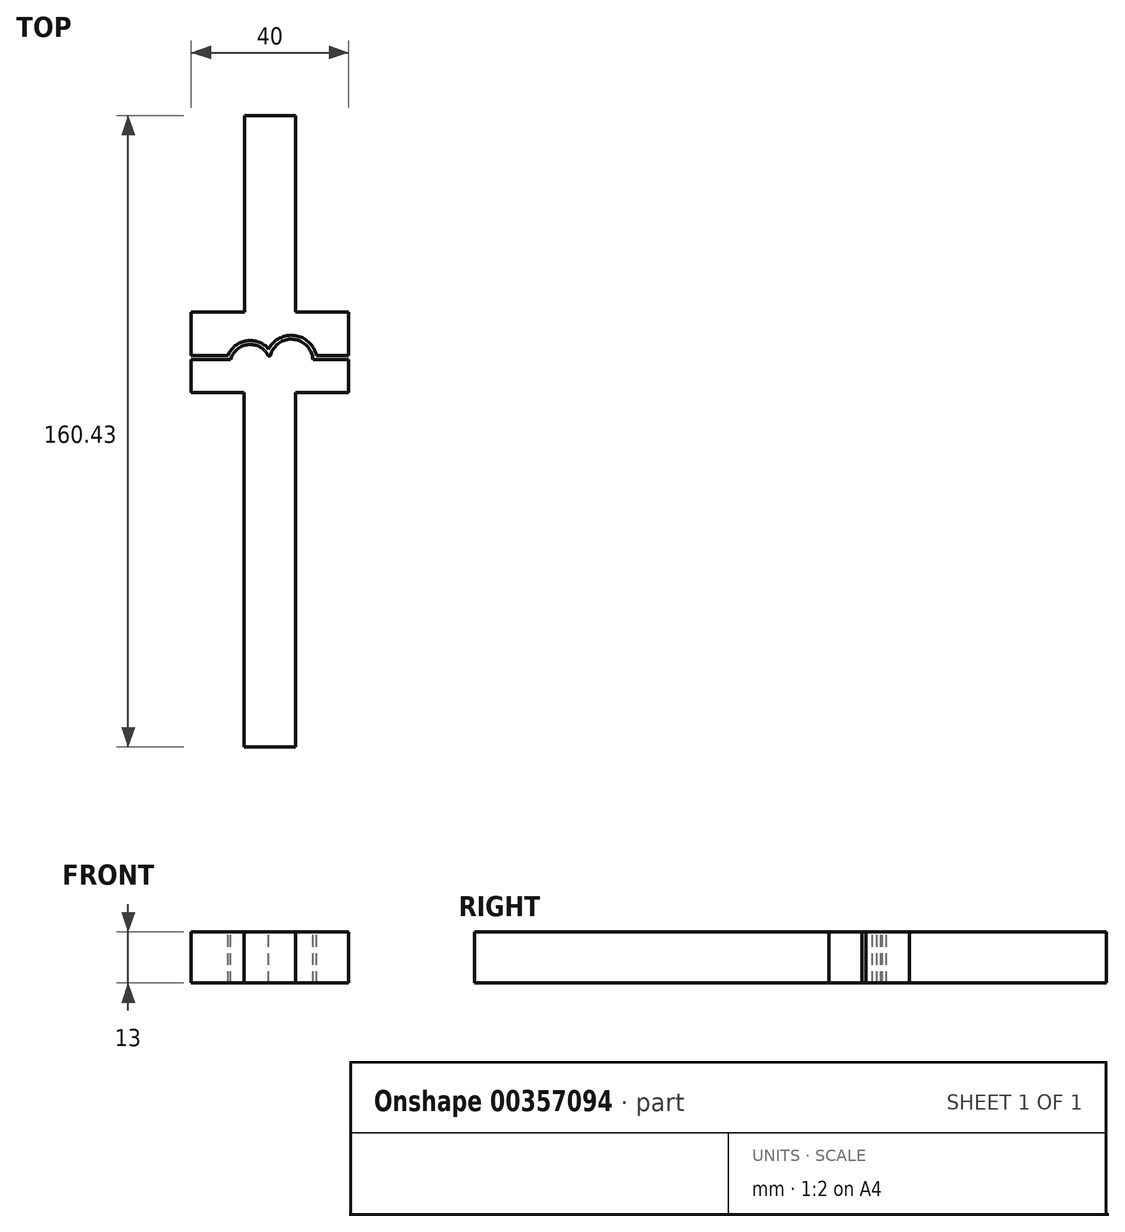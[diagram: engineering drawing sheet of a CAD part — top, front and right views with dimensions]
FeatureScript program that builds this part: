
annotation { "Feature Type Name" : "Feature", "Feature Type Description" : "" }
export const myFeature = defineFeature(function(context is Context, id is Id, definition is map)
    precondition{}
    {
        {
            var Q0;
            Q0=qCreatedBy(makeId("Top.planeOp"),FACE);
            var sketch = newSketch(context, id + "F0", { "sketchPlane" : qUnion([Q0])});
            skLineSegment(sketch, "E0", {"start": v(0, 0) * mm, "end": v(6.5, 0) * mm});
            skLineSegment(sketch, "E1", {"start": v(6.5, 0) * mm, "end": v(6.5, 90) * mm});
            skLineSegment(sketch, "E2", {"start": v(6.5, 90) * mm, "end": v(19.95, 90) * mm});
            skLineSegment(sketch, "E3", {"start": v(19.95, 90) * mm, "end": v(19.95, 98.43) * mm});
            skLineSegment(sketch, "E4.MirrorCS", {"start": v(-19.95, 90) * mm, "end": v(-19.95, 98.43) * mm});
            skLineSegment(sketch, "E5.MirrorCS", {"start": v(0, 0) * mm, "end": v(-6.5, 0) * mm});
            skLineSegment(sketch, "E6.MirrorCS", {"start": v(-6.5, 0) * mm, "end": v(-6.5, 90) * mm});
            skLineSegment(sketch, "E7.MirrorCS", {"start": v(-6.5, 90) * mm, "end": v(-19.95, 90) * mm});
            skLineSegment(sketch, "E8", {"start": v(-19.95, 98.43) * mm, "end": v(19.95, 98.43) * mm});
            skSolve(sketch);
        }
        {
            var Q0;
            Q0=makeQuery(id+"F0.imprint","IMPRINT",FACE,{"disambiguationData":[TD([[makeQuery(id+"F0.imprint","IMPRINT",EDGE,{"derivedFrom":sQuery(id+"F0.wireOp",EDGE,"E0")}),1.0]])]});
            extrude(context, id + "F1", {"entities" : qUnion([Q0]), "depth" : 13 * mm});
        }
        {
            var Q0;
            Q0=makeQuery(id+"F1.opExtrude","CAP_FACE",FACE,{"disambiguationData":[OSD([sQuery(id+"F0.wireOp",EDGE,"E0"),sQuery(id+"F0.wireOp",EDGE,"E1"),sQuery(id+"F0.wireOp",EDGE,"E2"),sQuery(id+"F0.wireOp",EDGE,"E3"),sQuery(id+"F0.wireOp",EDGE,"E4.MirrorCS"),sQuery(id+"F0.wireOp",EDGE,"E5.MirrorCS"),sQuery(id+"F0.wireOp",EDGE,"E6.MirrorCS"),sQuery(id+"F0.wireOp",EDGE,"E7.MirrorCS"),sQuery(id+"F0.wireOp",EDGE,"E8")])],"isStart":false});
            var sketch = newSketch(context, id + "F2", { "sketchPlane" : qUnion([Q0])});
            skArc(sketch, "E9", {"start": v(0, 98.43) * mm, "mid": v(-4.96, 102.24) * mm, "end": v(-9.92, 98.43) * mm});
            skArc(sketch, "E10", {"start": v(10.95, 98.43) * mm, "mid": v(5.48, 103.58) * mm, "end": v(0, 98.43) * mm});
            skSolve(sketch);
        }
        {
            var Q0;
            {var subQ0=sQuery(id+"F2.wireOp",EDGE,"E9");Q0=makeQuery(id+"F2.imprint","IMPRINT",FACE,{"disambiguationData":[TD([[makeQuery(id+"F2.imprint","IMPRINT",EDGE,{"derivedFrom":subQ0}),1.0]])]});}
            var Q1;
            {var subQ0=sQuery(id+"F2.wireOp",EDGE,"E10");Q1=makeQuery(id+"F2.imprint","IMPRINT",FACE,{"disambiguationData":[TD([[makeQuery(id+"F2.imprint","IMPRINT",EDGE,{"derivedFrom":subQ0}),1.0]])]});}
            var Q2;
            Q2=makeQuery(id+"F1.opExtrude","CAP_FACE",FACE,{"disambiguationData":[OSD([sQuery(id+"F0.wireOp",EDGE,"E0"),sQuery(id+"F0.wireOp",EDGE,"E1"),sQuery(id+"F0.wireOp",EDGE,"E2"),sQuery(id+"F0.wireOp",EDGE,"E3"),sQuery(id+"F0.wireOp",EDGE,"E4.MirrorCS"),sQuery(id+"F0.wireOp",EDGE,"E5.MirrorCS"),sQuery(id+"F0.wireOp",EDGE,"E6.MirrorCS"),sQuery(id+"F0.wireOp",EDGE,"E7.MirrorCS"),sQuery(id+"F0.wireOp",EDGE,"E8")])],"isStart":true});
            extrude(context, id + "F3", {"entities" : qUnion([Q0, Q1]), "operationType" : NewBodyOperationType.ADD, "oppositeDirection" : true, "endBoundEntityFace" : qUnion([Q2]), "depth" : 13 * mm});
        }
        {
            var Q0;
            {var subQ0=sQuery(id+"F2.wireOp",EDGE,"E10");var subQ1=sQuery(id+"F2.wireOp",EDGE,"E9");var subQ2=sQuery(id+"F0.wireOp",EDGE,"E8");Q0=makeQuery(id+"F3.boolean.opBoolean","MERGE",EDGE,{"derivedFrom":[makeQuery(id+"F3.opExtrude","SWEPT_EDGE",EDGE,{"disambiguationData":[OSD([subQ2,subQ1,subQ0]),ownerDisambiguation([makeQuery(id+"F2.imprint","IMPRINT",EDGE,{"derivedFrom":subQ1})])]}),makeQuery(id+"F3.opExtrude","SWEPT_EDGE",EDGE,{"disambiguationData":[OSD([subQ2,subQ1,subQ0]),ownerDisambiguation([makeQuery(id+"F2.imprint","IMPRINT",EDGE,{"derivedFrom":subQ0})])]})]});}
            fillet(context, id + "F4", {"entities" : qUnion([Q0]), "radius" : 0.3 * mm, "tangentPropagation" : true, "allowEdgeOverflow" : false});
        }
        {
            var Q0;
            {var subQ1=sQuery(id+"F0.wireOp",EDGE,"E8");var subQ5=sQuery(id+"F0.wireOp",EDGE,"E4.MirrorCS");Q0=makeQuery(id+"F3.boolean.opBoolean","SPLIT",FACE,{"disambiguationData":[TD([makeQuery(id+"F1.opExtrude","SWEPT_FACE",FACE,{"disambiguationData":[OSD([subQ5])]})])],"derivedFrom":makeQuery(id+"F1.opExtrude","SWEPT_FACE",FACE,{"disambiguationData":[OSD([subQ1])]})});}
            var sketch = newSketch(context, id + "F5", { "sketchPlane" : qUnion([Q0])});
            skLineSegment(sketch, "E11.bottom", {"start": v(19.95, 0) * mm, "end": v(-20.05, 0) * mm});
            skLineSegment(sketch, "E11.top", {"start": v(19.95, 13) * mm, "end": v(-20.05, 13) * mm});
            skLineSegment(sketch, "E11.left", {"start": v(19.95, 0) * mm, "end": v(19.95, 13) * mm});
            skLineSegment(sketch, "E11.right", {"start": v(-20.05, 0) * mm, "end": v(-20.05, 13) * mm});
            skSolve(sketch);
        }
        {
            var Q0;
            Q0 = qSketchRegion(id + "F5", true);
            extrude(context, id + "F6", {"entities" : qUnion([Q0]), "depth" : 12 * mm});
        }
        {
            var Q0;
            Q0=makeQuery(id+"F1.opExtrude","SWEPT_BODY",BODY,{"disambiguationData":[OSD([sQuery(id+"F0.wireOp",EDGE,"E0"),sQuery(id+"F0.wireOp",EDGE,"E1"),sQuery(id+"F0.wireOp",EDGE,"E2"),sQuery(id+"F0.wireOp",EDGE,"E3"),sQuery(id+"F0.wireOp",EDGE,"E4.MirrorCS"),sQuery(id+"F0.wireOp",EDGE,"E5.MirrorCS"),sQuery(id+"F0.wireOp",EDGE,"E6.MirrorCS"),sQuery(id+"F0.wireOp",EDGE,"E7.MirrorCS"),sQuery(id+"F0.wireOp",EDGE,"E8")])]});
            var Q1;
            Q1=makeQuery(id+"F6.opExtrude","SWEPT_BODY",BODY,{"disambiguationData":[OSD([sQuery(id+"F5.wireOp",EDGE,"E11.bottom"),sQuery(id+"F5.wireOp",EDGE,"E11.top"),sQuery(id+"F5.wireOp",EDGE,"E11.left"),sQuery(id+"F5.wireOp",EDGE,"E11.right")])]});
            var Q2;
            Q2=makeQuery(id+"F6.opExtrude","CAP_FACE",FACE,{"disambiguationData":[OSD([sQuery(id+"F5.wireOp",EDGE,"E11.bottom"),sQuery(id+"F5.wireOp",EDGE,"E11.top"),sQuery(id+"F5.wireOp",EDGE,"E11.left"),sQuery(id+"F5.wireOp",EDGE,"E11.right")])],"isStart":true});
            booleanBodies(context, id + "F7", {"operationType" : BooleanOperationType.SUBTRACTION, "tools" : qUnion([Q0]), "targets" : qUnion([Q1]), "offset" : true, "offsetAll" : true, "entitiesToOffset" : qUnion([Q2]), "offsetDistance" : 1 * mm, "keepTools" : true});
        }
        {
            var Q0;
            Q0=makeQuery(id+"F6.opExtrude","CAP_FACE",FACE,{"disambiguationData":[OSD([sQuery(id+"F5.wireOp",EDGE,"E11.bottom"),sQuery(id+"F5.wireOp",EDGE,"E11.top"),sQuery(id+"F5.wireOp",EDGE,"E11.left"),sQuery(id+"F5.wireOp",EDGE,"E11.right")])],"isStart":false});
            var sketch = newSketch(context, id + "F8", { "sketchPlane" : qUnion([Q0])});
            skLineSegment(sketch, "E12.bottom", {"start": v(6.45, 0) * mm, "end": v(-6.55, 0) * mm});
            skLineSegment(sketch, "E12.top", {"start": v(6.45, 13) * mm, "end": v(-6.55, 13) * mm});
            skLineSegment(sketch, "E12.left", {"start": v(6.45, 0) * mm, "end": v(6.45, 13) * mm});
            skLineSegment(sketch, "E12.right", {"start": v(-6.55, 0) * mm, "end": v(-6.55, 13) * mm});
            skSolve(sketch);
        }
        {
            var Q0;
            Q0 = qSketchRegion(id + "F8", true);
            extrude(context, id + "F9", {"entities" : qUnion([Q0]), "operationType" : NewBodyOperationType.ADD, "depth" : 50 * mm});
        }
    });
